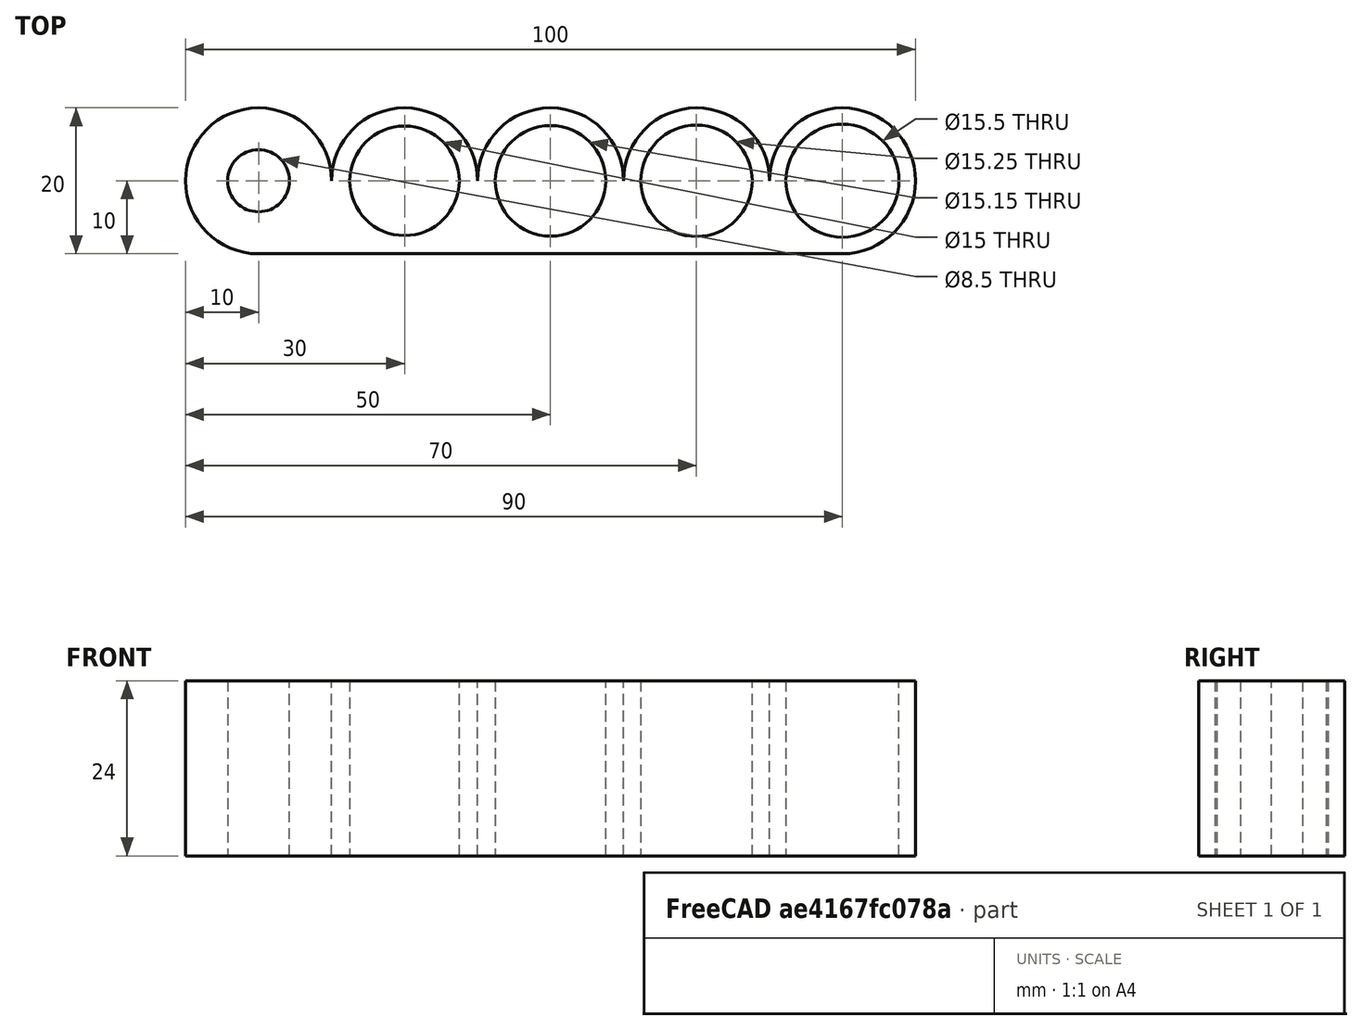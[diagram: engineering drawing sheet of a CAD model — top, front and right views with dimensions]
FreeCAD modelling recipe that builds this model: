
FCSTD DOCUMENT  (FreeCAD 1.0R39109 (Git))
Label: press_fit_test1
License: All rights reserved
LicenseURL: https://en.wikipedia.org/wiki/All_rights_reserved
objects: Sketcher::SketchObject×1, PartDesign::Pad×1, PartDesign::Body×1
note: 6 computed .brp shape members not serialized (recipe doc carries the construction recipe); baked Part::Feature solids carry a one-line shape summary decoded from their .brp

FEATURE [Sketcher::SketchObject] Sketch
  ArcFitTolerance = 1e-06
  AttachmentSupport = -> [XY_Plane]
  FullyConstrained = true
  MakeInternals = false
  MapMode = 5
  sketch-geometry (11):
    g0: ArcOfCircle CenterX=0 CenterY=0 CenterZ=0 NormalX=0 NormalY=0 NormalZ=1 AngleXU=0 Radius=10 StartAngle=0 EndAngle=4.71239
    g1: ArcOfCircle CenterX=20 CenterY=0 CenterZ=0 NormalX=0 NormalY=0 NormalZ=1 AngleXU=0 Radius=10 StartAngle=0 EndAngle=3.14159
    g2: ArcOfCircle CenterX=40 CenterY=0 CenterZ=0 NormalX=0 NormalY=0 NormalZ=1 AngleXU=0 Radius=10 StartAngle=0 EndAngle=3.14159
    g3: ArcOfCircle CenterX=60 CenterY=0 CenterZ=0 NormalX=0 NormalY=0 NormalZ=1 AngleXU=0 Radius=10 StartAngle=1e-16 EndAngle=3.14159
    g4: ArcOfCircle CenterX=80 CenterY=0 CenterZ=0 NormalX=0 NormalY=0 NormalZ=1 AngleXU=0 Radius=10 StartAngle=4.71239 EndAngle=9.42478
    g5: Circle CenterX=0 CenterY=0 CenterZ=0 NormalX=0 NormalY=0 NormalZ=1 AngleXU=0 Radius=4.25
    g6: Circle CenterX=20 CenterY=0 CenterZ=0 NormalX=0 NormalY=0 NormalZ=1 AngleXU=0 Radius=7.5
    g7: Circle CenterX=40 CenterY=0 CenterZ=0 NormalX=0 NormalY=0 NormalZ=1 AngleXU=0 Radius=7.575
    g8: Circle CenterX=60 CenterY=0 CenterZ=0 NormalX=0 NormalY=0 NormalZ=1 AngleXU=0 Radius=7.625
    g9: Circle CenterX=80 CenterY=0 CenterZ=0 NormalX=0 NormalY=0 NormalZ=1 AngleXU=0 Radius=7.75
    g10: LineSegment StartX=80 StartY=-10 StartZ=0 EndX=-5.969e-13 EndY=-10 EndZ=0
  constraints (27):
    c: Coincident(g0,g-1)
    c: PointOnObject(g1,g-1)
    c: PointOnObject(g2,g-1)
    c: PointOnObject(g3,g-1)
    c: PointOnObject(g4,g-1)
    c: Diameter(g0) = 20
    c: Equal(g1,g0)
    c: Equal(g0,g2)
    c: Equal(g2,g3)
    c: Equal(g3,g4)
    c: Diameter(g5) = 8.5
    c: Diameter(g6) = 15
    c: Coincident(g6,g1)
    c: Coincident(g5,g0)
    c: Diameter(g7) = 15.15
    c: Coincident(g7,g2)
    c: Diameter(g8) = 15.25
    c: Coincident(g8,g3)
    c: Diameter(g9) = 15.5
    c: Coincident(g9,g4)
    c: Tangent(g0,g10) = 1.5708
    c: Tangent(g1,g0) = 1.5708
    c: Tangent(g2,g1) = 1.5708
    c: Tangent(g3,g2) = 1.5708
    c: Coincident(g4,g10)
    c: Tangent(g3,g4) = 1.5708
    c: Angle(g4) = 4.71239
FEATURE [PartDesign::Pad] Pad
  Direction = (0,0,1)
  Length = 24
  Length2 = 10
  Profile = -> Sketch
  ReferenceAxis = -> Sketch [N_Axis]
  Refine = true
  Suppressed = false
  Type = 0
FEATURE [PartDesign::Body] Body
  AllowCompound = false
  Group = -> [Sketch,Pad]
  Origin = -> Origin
  Tip = -> Pad
